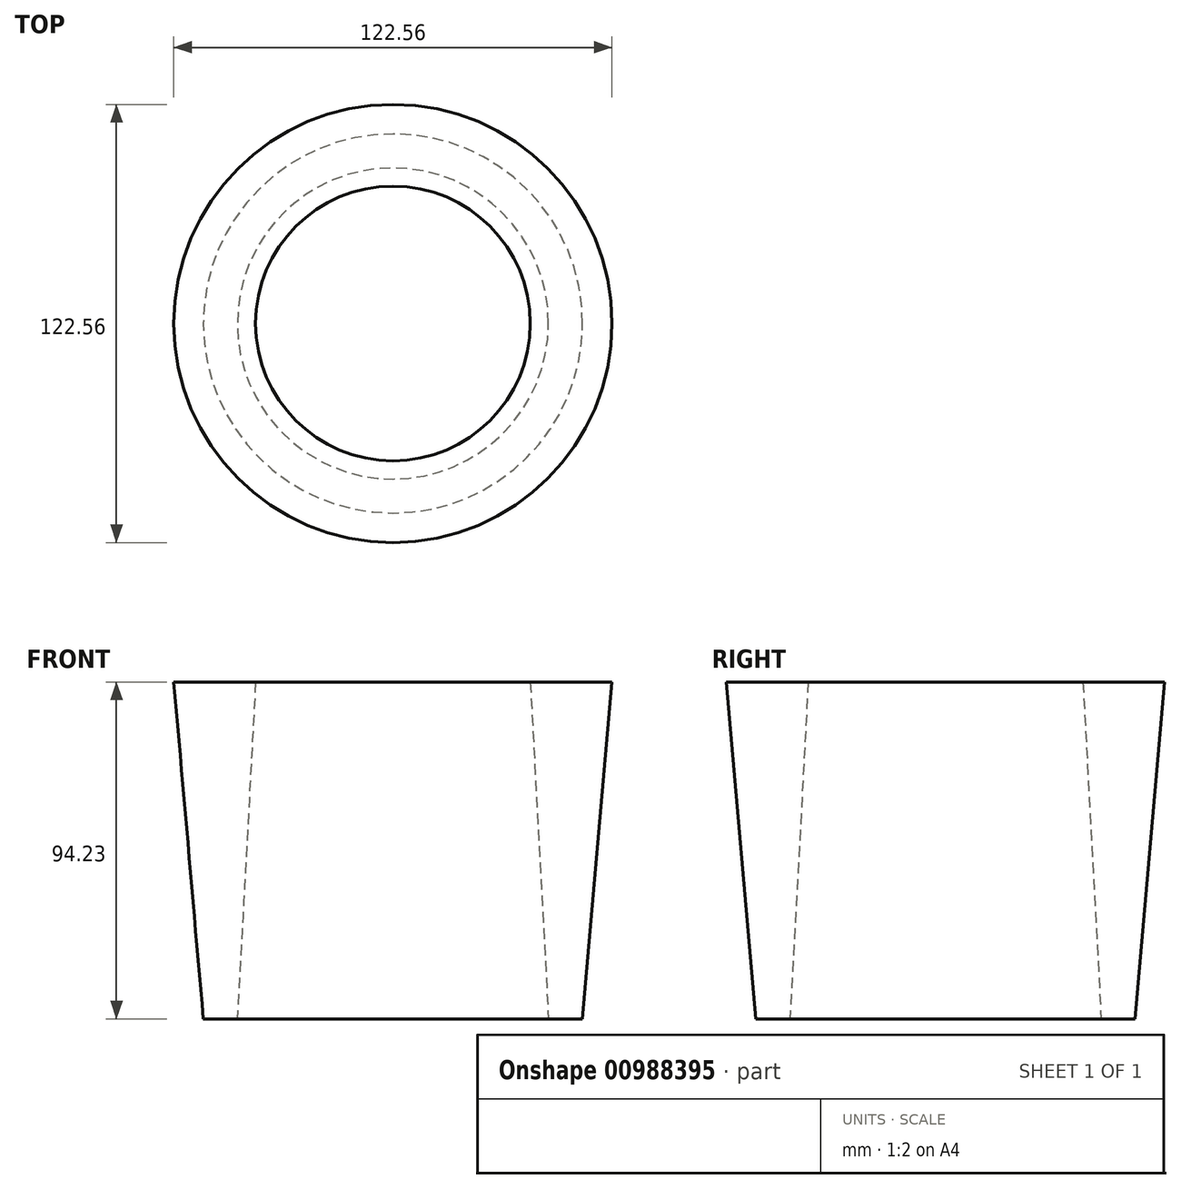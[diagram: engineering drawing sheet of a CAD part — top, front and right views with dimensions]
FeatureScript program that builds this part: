
annotation { "Feature Type Name" : "Feature", "Feature Type Description" : "" }
export const myFeature = defineFeature(function(context is Context, id is Id, definition is map)
    precondition{}
    {
        {
            var Q0;
            Q0=qCreatedBy(makeId("Front.planeOp"),FACE);
            var sketch = newSketch(context, id + "F0", { "sketchPlane" : qUnion([Q0])});
            skLineSegment(sketch, "E0", {"start": v(0, 0) * mm, "end": v(0, 44.65) * mm, "construction": true});
            skLineSegment(sketch, "E1", {"start": v(-61.28, 51.18) * mm, "end": v(-53.02, -43.05) * mm});
            skLineSegment(sketch, "E2", {"start": v(-53.02, -43.05) * mm, "end": v(-43.5, -43.05) * mm});
            skLineSegment(sketch, "E3", {"start": v(-53.02, -43.05) * mm, "end": v(0, -43.05) * mm, "construction": true});
            skLineSegment(sketch, "E4", {"start": v(-61.28, 51.18) * mm, "end": v(0, 51.18) * mm, "construction": true});
            skLineSegment(sketch, "E5", {"start": v(-43.5, 51.18) * mm, "end": v(-38.42, 51.18) * mm});
            skLineSegment(sketch, "E6", {"start": v(-61.28, 51.18) * mm, "end": v(-38.42, 51.18) * mm});
            skLineSegment(sketch, "E7", {"start": v(-38.42, 51.18) * mm, "end": v(-43.5, -43.05) * mm});
            skLineSegment(sketch, "E8", {"start": v(-38.42, 51.18) * mm, "end": v(-38.42, -43.05) * mm, "construction": true});
            skSolve(sketch);
        }
        {
            var Q0;
            Q0=makeQuery(id+"F0.imprint","IMPRINT",FACE,{"disambiguationData":[TD([[makeQuery(id+"F0.imprint","IMPRINT",EDGE,{"derivedFrom":sQuery(id+"F0.wireOp",EDGE,"E1")}),1.0]])]});
            var Q1;
            Q1=sQuery(id+"F0.wireOp",EDGE,"E0");
            revolve(context, id + "F1", {"surfaceOperationType" : NewSurfaceOperationType.NEW, "entities" : qUnion([Q0]), "axis" : qUnion([Q1]), "revolveType" : RevolveType.FULL});
        }
    });
